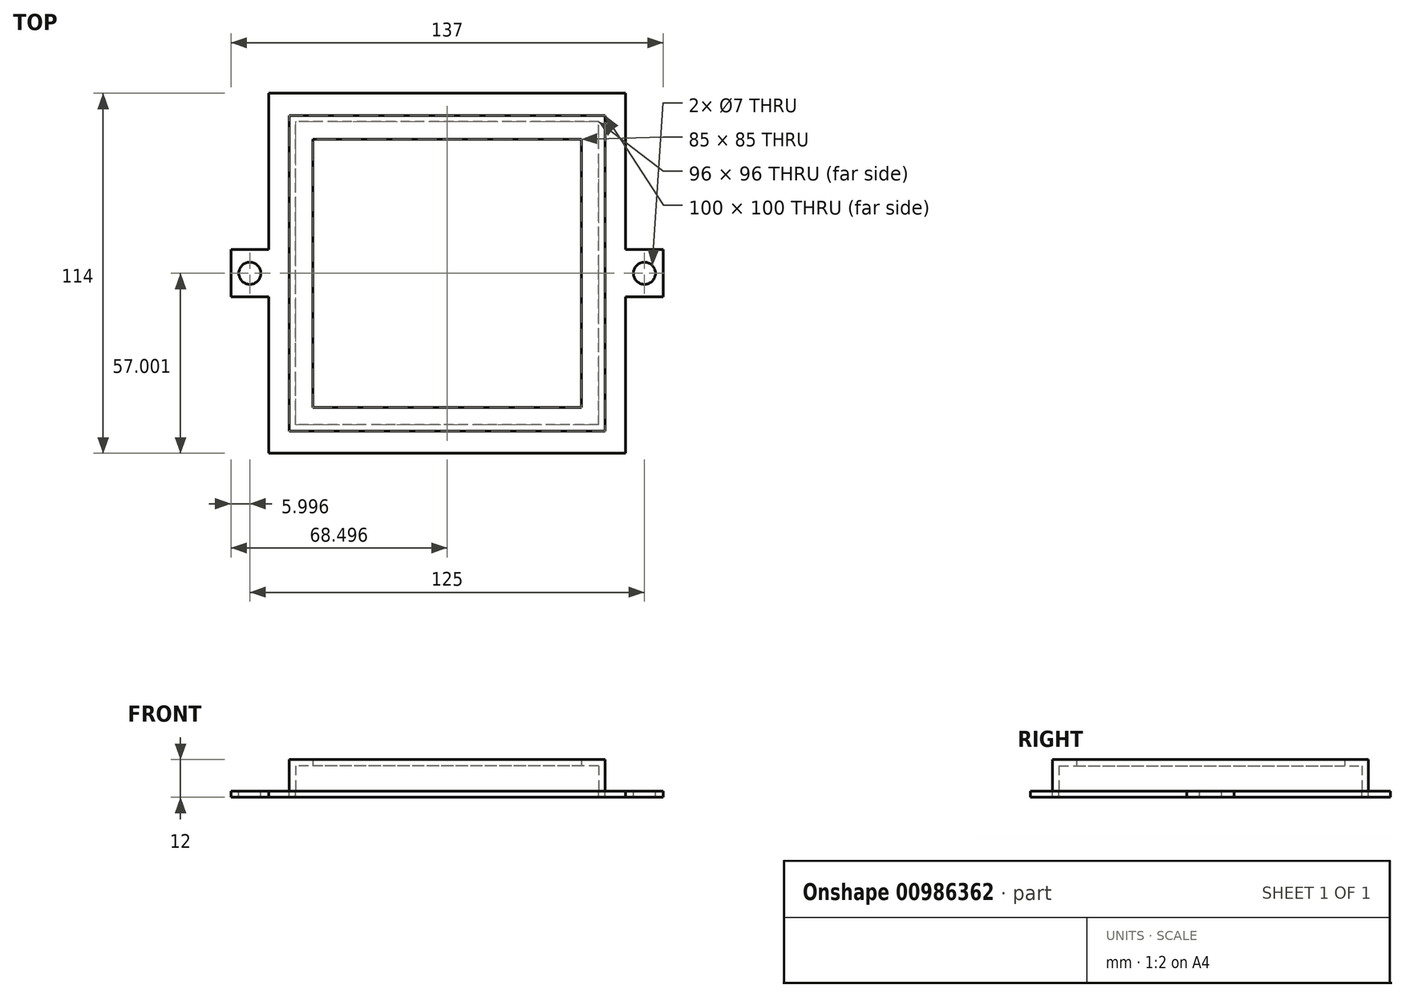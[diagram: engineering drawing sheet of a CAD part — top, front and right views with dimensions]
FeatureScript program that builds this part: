
annotation { "Feature Type Name" : "Feature", "Feature Type Description" : "" }
export const myFeature = defineFeature(function(context is Context, id is Id, definition is map)
    precondition{}
    {
        {
            var Q0;
            Q0=qCreatedBy(makeId("Top.planeOp"),FACE);
            var sketch = newSketch(context, id + "F0", { "sketchPlane" : qUnion([Q0])});
            skLineSegment(sketch, "E0.bottom", {"start": v(74.05, -82.42) * mm, "end": v(-38.95, -82.42) * mm});
            skLineSegment(sketch, "E0.top", {"start": v(74.05, 31.58) * mm, "end": v(-38.95, 31.58) * mm});
            skLineSegment(sketch, "E0.left", {"start": v(74.05, -82.42) * mm, "end": v(74.05, 31.58) * mm});
            skLineSegment(sketch, "E0.right", {"start": v(-38.95, -82.42) * mm, "end": v(-38.95, 31.58) * mm});
            skPoint(sketch, "E0.middle", {"position": v(17.55, -25.42) * mm});
            skLineSegment(sketch, "E1.bottom", {"start": v(67.55, -75.42) * mm, "end": v(-32.45, -75.42) * mm});
            skLineSegment(sketch, "E1.top", {"start": v(67.55, 24.58) * mm, "end": v(-32.45, 24.58) * mm});
            skLineSegment(sketch, "E1.left", {"start": v(67.55, -75.42) * mm, "end": v(67.55, 24.58) * mm});
            skLineSegment(sketch, "E1.right", {"start": v(-32.45, -75.42) * mm, "end": v(-32.45, 24.58) * mm});
            skLineSegment(sketch, "E2.bottom", {"start": v(65.55, -73.42) * mm, "end": v(-30.45, -73.42) * mm});
            skLineSegment(sketch, "E2.top", {"start": v(65.55, 22.58) * mm, "end": v(-30.45, 22.58) * mm});
            skLineSegment(sketch, "E2.left", {"start": v(65.55, -73.42) * mm, "end": v(65.55, 22.58) * mm});
            skLineSegment(sketch, "E2.right", {"start": v(-30.45, -73.42) * mm, "end": v(-30.45, 22.58) * mm});
            skLineSegment(sketch, "E3.bottom", {"start": v(60.05, -67.92) * mm, "end": v(-24.95, -67.92) * mm});
            skLineSegment(sketch, "E3.top", {"start": v(60.05, 17.08) * mm, "end": v(-24.95, 17.08) * mm});
            skLineSegment(sketch, "E3.left", {"start": v(60.05, -67.92) * mm, "end": v(60.05, 17.08) * mm});
            skLineSegment(sketch, "E3.right", {"start": v(-24.95, -67.92) * mm, "end": v(-24.95, 17.08) * mm});
            skLineSegment(sketch, "E4", {"start": v(-32.45, 24.58) * mm, "end": v(-38.95, 31.58) * mm});
            skLineSegment(sketch, "E5", {"start": v(-32.45, -75.42) * mm, "end": v(-38.95, -82.42) * mm});
            skLineSegment(sketch, "E6", {"start": v(67.55, -75.42) * mm, "end": v(74.05, -82.42) * mm});
            skLineSegment(sketch, "E7", {"start": v(74.05, 31.58) * mm, "end": v(67.55, 24.58) * mm});
            skLineSegment(sketch, "E8", {"start": v(17.55, 31.58) * mm, "end": v(17.55, 24.58) * mm});
            skPoint(sketch, "E9", {"position": v(17.55, 28.08) * mm});
            skLineSegment(sketch, "E10", {"start": v(74.05, -25.42) * mm, "end": v(67.55, -25.42) * mm});
            skPoint(sketch, "E11", {"position": v(70.8, -25.42) * mm});
            skLineSegment(sketch, "E12", {"start": v(17.55, -75.42) * mm, "end": v(17.55, -82.42) * mm});
            skLineSegment(sketch, "E13", {"start": v(-32.45, -25.42) * mm, "end": v(-38.95, -25.42) * mm});
            skPoint(sketch, "E14", {"position": v(-35.7, -25.42) * mm});
            skPoint(sketch, "E15", {"position": v(17.55, -78.92) * mm});
            skLineSegment(sketch, "E16", {"start": v(-38.95, -25.42) * mm, "end": v(-44.95, -25.42) * mm});
            skLineSegment(sketch, "E17.bottom", {"start": v(-38.95, -32.92) * mm, "end": v(-50.95, -32.92) * mm});
            skLineSegment(sketch, "E17.top", {"start": v(-38.95, -17.92) * mm, "end": v(-50.95, -17.92) * mm});
            skLineSegment(sketch, "E17.left", {"start": v(-38.95, -32.92) * mm, "end": v(-38.95, -17.92) * mm});
            skLineSegment(sketch, "E17.right", {"start": v(-50.95, -32.92) * mm, "end": v(-50.95, -17.92) * mm});
            skPoint(sketch, "E17.middle", {"position": v(-44.95, -25.42) * mm});
            skCircle(sketch, "E18", {"center": v(-44.95, -25.42) * mm, "radius": 3.5 * mm});
            skLineSegment(sketch, "E19", {"start": v(74.05, -25.42) * mm, "end": v(80.05, -25.42) * mm});
            skLineSegment(sketch, "E20.bottom", {"start": v(74.05, -32.92) * mm, "end": v(86.05, -32.92) * mm});
            skLineSegment(sketch, "E20.top", {"start": v(74.05, -17.92) * mm, "end": v(86.05, -17.92) * mm});
            skLineSegment(sketch, "E20.left", {"start": v(74.05, -32.92) * mm, "end": v(74.05, -17.92) * mm});
            skLineSegment(sketch, "E20.right", {"start": v(86.05, -32.92) * mm, "end": v(86.05, -17.92) * mm});
            skPoint(sketch, "E20.middle", {"position": v(80.05, -25.42) * mm});
            skCircle(sketch, "E21", {"center": v(80.05, -25.42) * mm, "radius": 3.5 * mm});
            skSolve(sketch);
        }
        {
            var Q0;
            Q0 = qSketchRegion(id + "F0", true);
            extrude(context, id + "F1", {"entities" : qUnion([Q0]), "oppositeDirection" : true, "depth" : 2 * mm, "offsetDistance" : 25 * mm});
        }
        {
            var Q0;
            Q0=makeQuery(id+"F0.imprint","IMPRINT",FACE,{"disambiguationData":[TD([[makeQuery(id+"F0.imprint","IMPRINT",EDGE,{"derivedFrom":sQuery(id+"F0.wireOp",EDGE,"E2.bottom")}),-1.0]])]});
            var Q1;
            Q1=makeQuery(id+"F0.imprint","IMPRINT",FACE,{"disambiguationData":[TD([[makeQuery(id+"F0.imprint","IMPRINT",EDGE,{"derivedFrom":sQuery(id+"F0.wireOp",EDGE,"E2.bottom")}),1.0]])]});
            extrude(context, id + "F2", {"entities" : qUnion([Q0, Q1]), "operationType" : NewBodyOperationType.ADD, "depth" : 10 * mm, "offsetDistance" : 25 * mm});
        }
        {
            var Q0;
            Q0=makeQuery(id+"F0.imprint","IMPRINT",FACE,{"disambiguationData":[TD([[makeQuery(id+"F0.imprint","IMPRINT",EDGE,{"derivedFrom":sQuery(id+"F0.wireOp",EDGE,"E2.bottom")}),-1.0]])]});
            extrude(context, id + "F3", {"entities" : qUnion([Q0]), "operationType" : NewBodyOperationType.REMOVE, "depth" : 8 * mm, "offsetDistance" : 25 * mm});
        }
        {
            var Q0;
            Q0=makeQuery(id+"F0.imprint","IMPRINT",FACE,{"disambiguationData":[TD([[makeQuery(id+"F0.imprint","IMPRINT",EDGE,{"derivedFrom":sQuery(id+"F0.wireOp",EDGE,"E2.bottom")}),1.0]])]});
            extrude(context, id + "F4", {"entities" : qUnion([Q0]), "oppositeDirection" : true, "depth" : 2 * mm, "offsetDistance" : 25 * mm});
        }
    });
